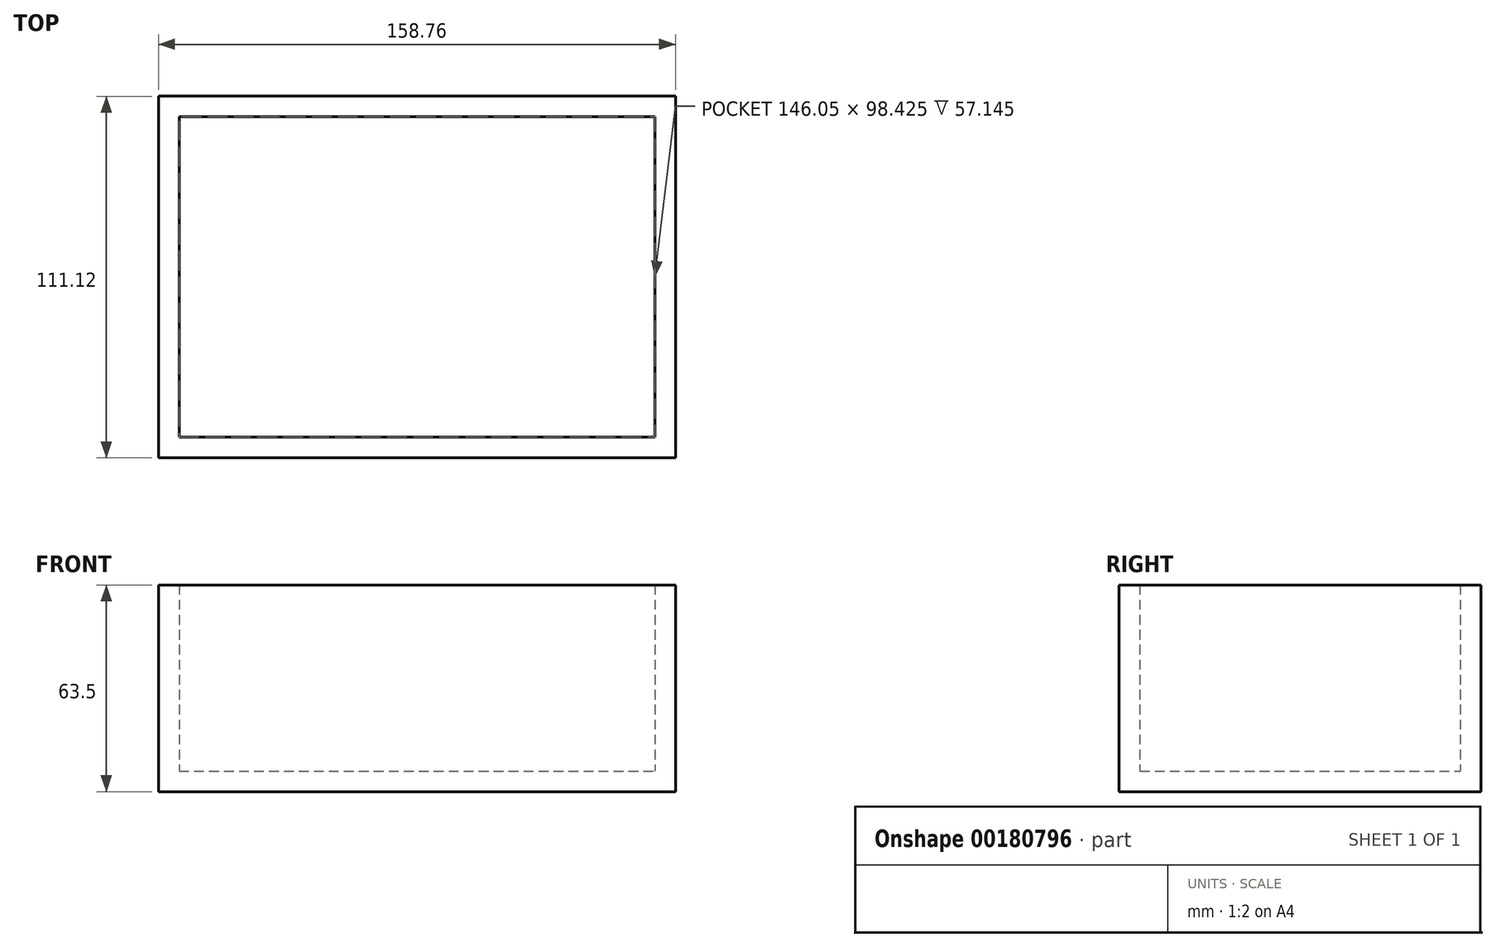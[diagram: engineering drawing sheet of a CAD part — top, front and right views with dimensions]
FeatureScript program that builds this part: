
annotation { "Feature Type Name" : "Feature", "Feature Type Description" : "" }
export const myFeature = defineFeature(function(context is Context, id is Id, definition is map)
    precondition{}
    {
        {
            assignVariable(context, id + "F0", {"name" : "box_height", "anyValue" : 57.15 * mm});
        }
        {
            assignVariable(context, id + "F1", {"name" : "wall_thickness", "anyValue" : 6.35 * mm});
        }
        {
            var Q0;
            Q0=qCreatedBy(makeId("Top.planeOp"),FACE);
            var sketch = newSketch(context, id + "F2", { "sketchPlane" : qUnion([Q0])});
            skLineSegment(sketch, "E0.bottom", {"start": v(79.38, 55.56) * mm, "end": v(-79.37, 55.56) * mm});
            skLineSegment(sketch, "E0.top", {"start": v(79.38, -55.56) * mm, "end": v(-79.38, -55.56) * mm});
            skLineSegment(sketch, "E0.left", {"start": v(79.38, 55.56) * mm, "end": v(79.38, -55.56) * mm});
            skLineSegment(sketch, "E0.right", {"start": v(-79.37, 55.56) * mm, "end": v(-79.38, -55.56) * mm});
            skPoint(sketch, "E0.middle", {"position": v(0, 0) * mm});
            skSolve(sketch);
        }
        {
            var Q0;
            Q0=makeQuery(id+"F2.imprint","IMPRINT",FACE,{"disambiguationData":[TD([[makeQuery(id+"F2.imprint","IMPRINT",EDGE,{"derivedFrom":sQuery(id+"F2.wireOp",EDGE,"E0.bottom")}),1.0]])]});
            extrude(context, id + "F3", {"entities" : qUnion([Q0]), "depth" : getVariable(context, 'wall_thickness')});
        }
        {
            var Q0;
            Q0=makeQuery(id+"F3.opExtrude","CAP_FACE",FACE,{"disambiguationData":[OSD([sQuery(id+"F2.wireOp",EDGE,"E0.bottom"),sQuery(id+"F2.wireOp",EDGE,"E0.top"),sQuery(id+"F2.wireOp",EDGE,"E0.left"),sQuery(id+"F2.wireOp",EDGE,"E0.right")])],"isStart":false});
            var sketch = newSketch(context, id + "F4", { "sketchPlane" : qUnion([Q0])});
            skLineSegment(sketch, "E1.bottom", {"start": v(-79.37, 55.56) * mm, "end": v(79.37, 55.56) * mm});
            skLineSegment(sketch, "E1.top", {"start": v(-79.38, -55.56) * mm, "end": v(79.37, -55.56) * mm});
            skLineSegment(sketch, "E1.left", {"start": v(-79.38, 55.56) * mm, "end": v(-79.38, -55.56) * mm});
            skLineSegment(sketch, "E1.right", {"start": v(79.38, 55.56) * mm, "end": v(79.37, -55.56) * mm});
            skPoint(sketch, "E1.middle", {"position": v(0, 0) * mm});
            skLineSegment(sketch, "E2.0", {"start": v(73.03, -49.21) * mm, "end": v(73.03, 49.21) * mm});
            skLineSegment(sketch, "E2.1", {"start": v(-73.03, -49.21) * mm, "end": v(73.03, -49.21) * mm});
            skLineSegment(sketch, "E2.2", {"start": v(-73.02, 49.21) * mm, "end": v(-73.03, -49.21) * mm});
            skLineSegment(sketch, "E2.3", {"start": v(73.03, 49.21) * mm, "end": v(-73.03, 49.21) * mm});
            skSolve(sketch);
        }
        {
            var Q0;
            Q0 = qSketchRegion(id + "F4", true);
            extrude(context, id + "F5", {"entities" : qUnion([Q0]), "operationType" : NewBodyOperationType.ADD, "depth" : (getVariable(context, 'box_height') - 1 / 203.2 * mm), "offsetDistance" : 25 * mm});
        }
    });
